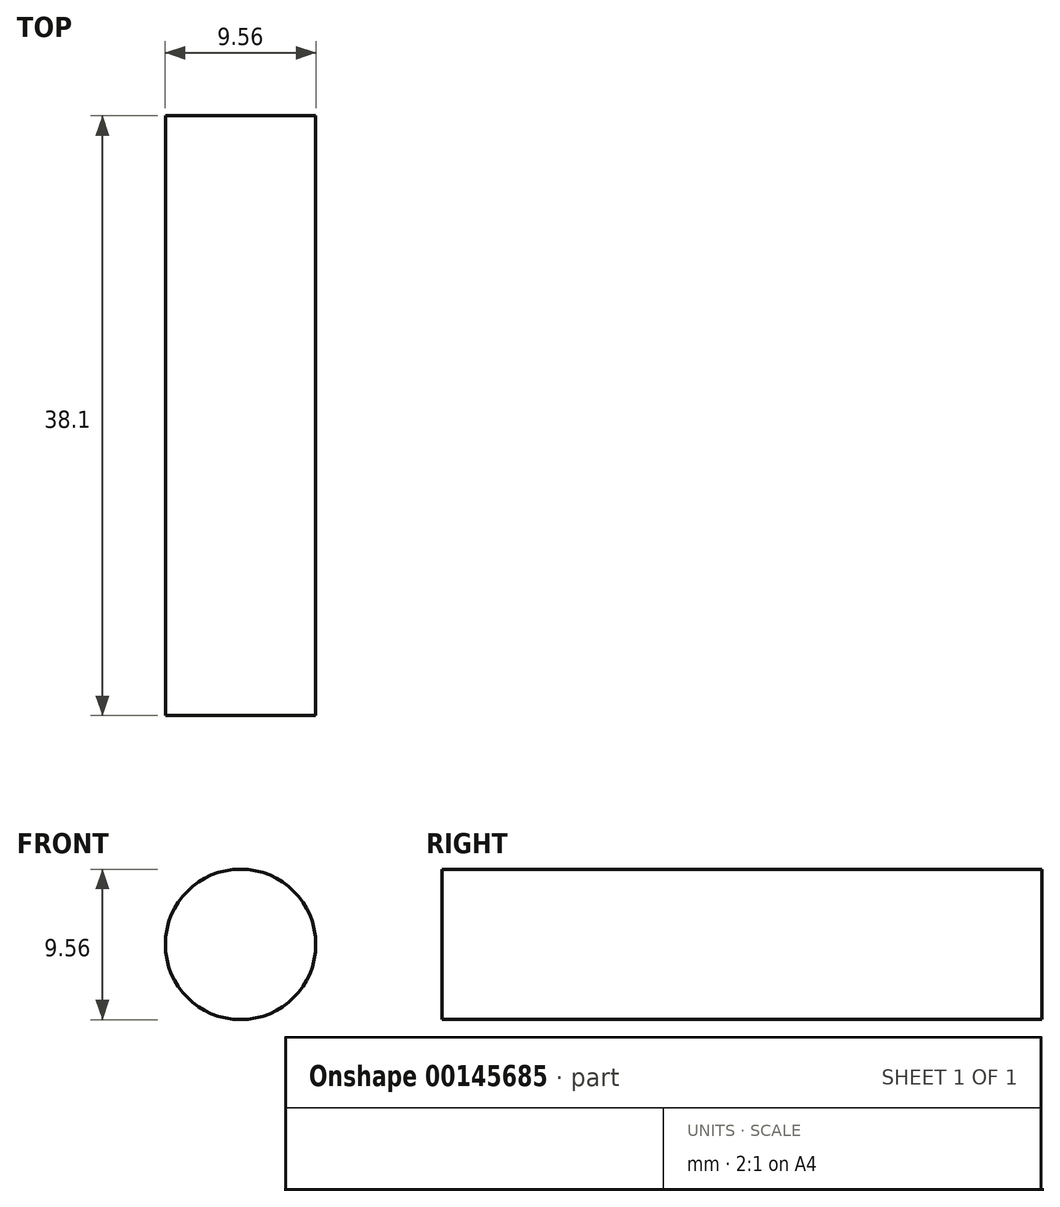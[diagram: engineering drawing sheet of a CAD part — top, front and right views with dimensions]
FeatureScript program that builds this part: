
annotation { "Feature Type Name" : "Feature", "Feature Type Description" : "" }
export const myFeature = defineFeature(function(context is Context, id is Id, definition is map)
    precondition{}
    {
        {
            var Q0;
            Q0=qCreatedBy(makeId("Front.planeOp"),FACE);
            var sketch = newSketch(context, id + "F0", { "sketchPlane" : qUnion([Q0])});
            skCircle(sketch, "E0", {"center": v(0, 0) * mm, "radius": 4.78 * mm});
            skSolve(sketch);
        }
        {
            var Q0;
            Q0 = qSketchRegion(id + "F0", true);
            extrude(context, id + "F1", {"entities" : qUnion([Q0]), "depth" : 38.1 * mm});
        }
    });
